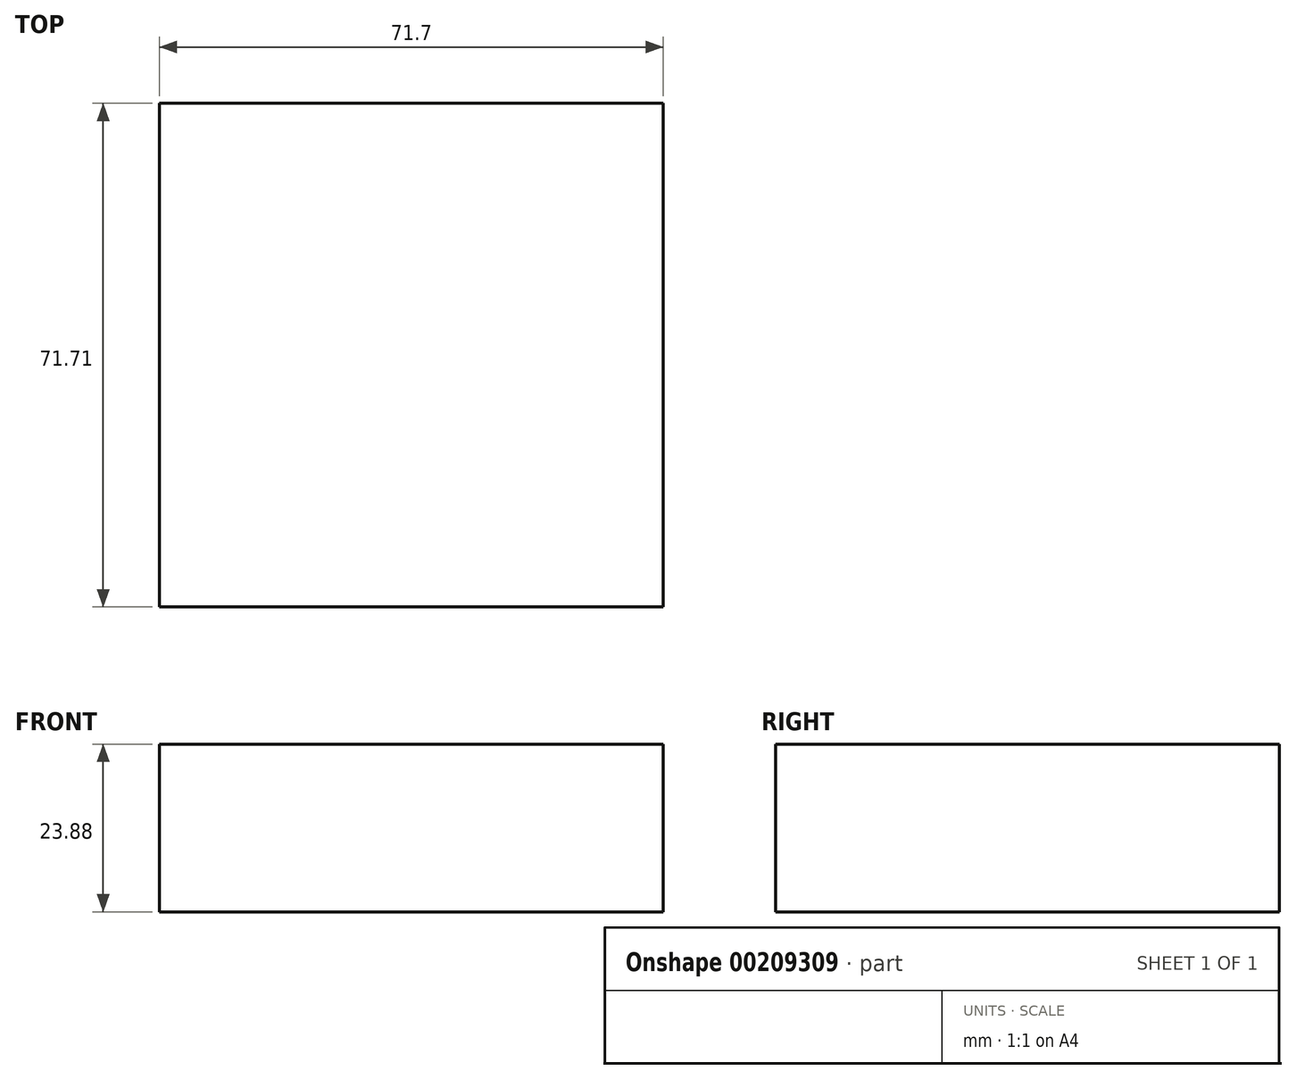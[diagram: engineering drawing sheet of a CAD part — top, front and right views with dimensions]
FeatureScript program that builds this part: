
annotation { "Feature Type Name" : "Feature", "Feature Type Description" : "" }
export const myFeature = defineFeature(function(context is Context, id is Id, definition is map)
    precondition{}
    {
        {
            var Q0;
            Q0=qCreatedBy(makeId("Top.planeOp"),FACE);
            var sketch = newSketch(context, id + "F0", { "sketchPlane" : qUnion([Q0])});
            skLineSegment(sketch, "E0.bottom", {"start": v(-35.76, 17.93) * mm, "end": v(35.94, 17.93) * mm});
            skLineSegment(sketch, "E0.top", {"start": v(-35.76, -53.78) * mm, "end": v(35.94, -53.78) * mm});
            skLineSegment(sketch, "E0.left", {"start": v(-35.76, 17.93) * mm, "end": v(-35.76, -53.78) * mm});
            skLineSegment(sketch, "E0.right", {"start": v(35.94, 17.93) * mm, "end": v(35.94, -53.78) * mm});
            skSolve(sketch);
        }
        {
            var Q0;
            Q0=makeQuery(id+"F0.imprint","IMPRINT",FACE,{"disambiguationData":[TD([[makeQuery(id+"F0.imprint","IMPRINT",EDGE,{"derivedFrom":sQuery(id+"F0.wireOp",EDGE,"E0.bottom")}),-1.0]])]});
            extrude(context, id + "F1", {"entities" : qUnion([Q0]), "depth" : 23.88 * mm});
        }
    });
